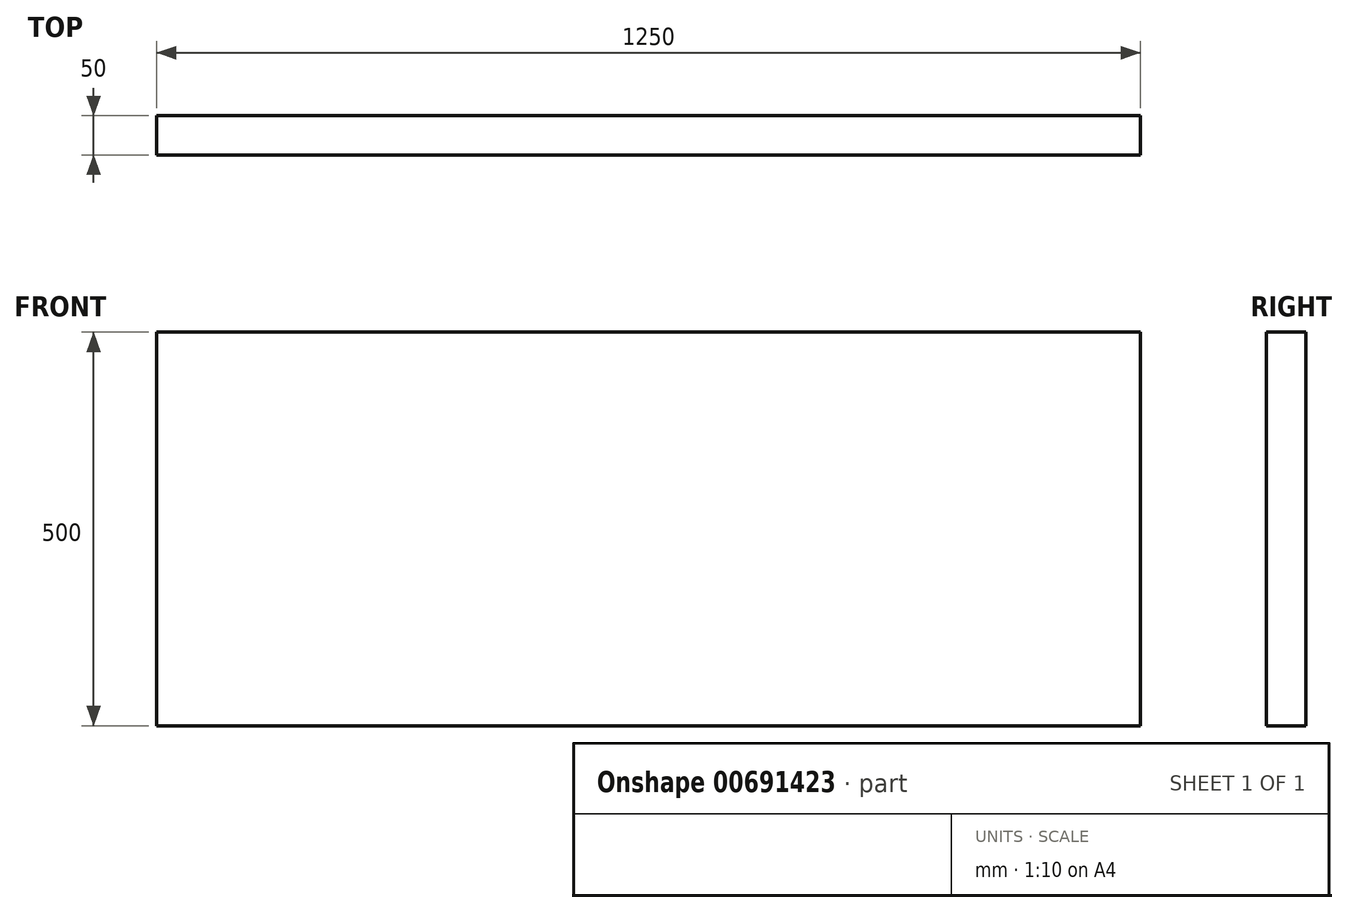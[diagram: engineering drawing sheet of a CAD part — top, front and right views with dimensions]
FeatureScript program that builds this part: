
annotation { "Feature Type Name" : "Feature", "Feature Type Description" : "" }
export const myFeature = defineFeature(function(context is Context, id is Id, definition is map)
    precondition{}
    {
        {
            var Q0;
            Q0=qCreatedBy(makeId("Front.planeOp"),FACE);
            var sketch = newSketch(context, id + "F0", { "sketchPlane" : qUnion([Q0])});
            skLineSegment(sketch, "E0.bottom", {"start": v(629.04, 250) * mm, "end": v(-620.96, 250) * mm});
            skLineSegment(sketch, "E0.top", {"start": v(629.04, -250) * mm, "end": v(-620.96, -250) * mm});
            skLineSegment(sketch, "E0.left", {"start": v(629.04, 250) * mm, "end": v(629.04, -250) * mm});
            skLineSegment(sketch, "E0.right", {"start": v(-620.96, 250) * mm, "end": v(-620.96, -250) * mm});
            skPoint(sketch, "E0.middle", {"position": v(4.04, 0) * mm});
            skSolve(sketch);
        }
        {
            var Q0;
            Q0 = qSketchRegion(id + "F0", true);
            extrude(context, id + "F1", {"entities" : qUnion([Q0]), "depth" : 50 * mm, "offsetDistance" : 25 * mm});
        }
    });
